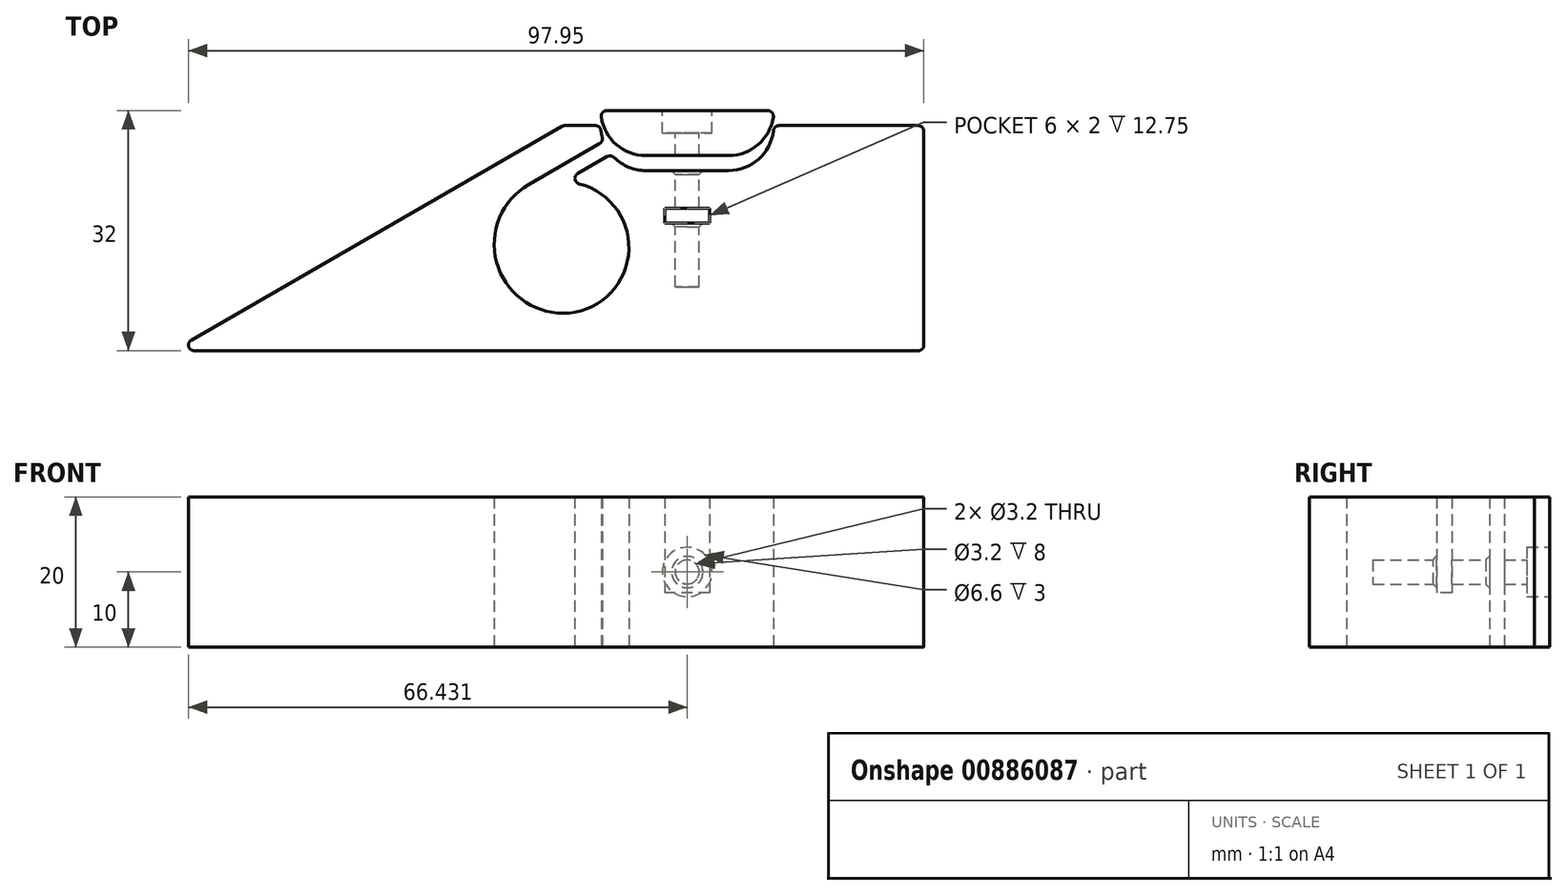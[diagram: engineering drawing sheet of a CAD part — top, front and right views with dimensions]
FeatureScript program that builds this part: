
annotation { "Feature Type Name" : "Feature", "Feature Type Description" : "" }
export const myFeature = defineFeature(function(context is Context, id is Id, definition is map)
    precondition{}
    {
        {
            assignVariable(context, id + "F0", {"name" : "distance", "anyValue" : 2});
        }
        {
            assignVariable(context, id + "F1", {"name" : "depth", "anyValue" : 20});
        }
        {
            assignVariable(context, id + "F2", {"name" : "squareNutWidth", "anyValue" : 5.5});
        }
        {
            var Q0;
            Q0=qCreatedBy(makeId("Top.planeOp"),FACE);
            var sketch = newSketch(context, id + "F3", { "sketchPlane" : qUnion([Q0])});
            skLineSegment(sketch, "E0", {"start": v(2.42, 1.4) * mm, "end": v(51.79, 29.9) * mm});
            skLineSegment(sketch, "E1", {"start": v(52.16, 30) * mm, "end": v(56.25, 30) * mm});
            skLineSegment(sketch, "E2", {"start": v(51.96, 30) * mm, "end": v(51.96, 0) * mm, "construction": true});
            skLineSegment(sketch, "E3", {"start": v(2.8, 0) * mm, "end": v(99.25, 0) * mm});
            skLineSegment(sketch, "E4", {"start": v(100, 0.75) * mm, "end": v(100, 29.25) * mm});
            skLineSegment(sketch, "E5", {"start": v(99.25, 30) * mm, "end": v(80.7, 30) * mm});
            skArc(sketch, "E6", {"start": v(57, 29.33) * mm, "mid": v(57.07, 28.89) * mm, "end": v(57.17, 28.45) * mm});
            skArc(sketch, "E7", {"start": v(74, 24) * mm, "mid": v(78, 25.53) * mm, "end": v(79.96, 29.33) * mm});
            skPoint(sketch, "E8.centerSnap0", {"position": v(100, 15) * mm});
            skPoint(sketch, "E8.centerSnap1", {"position": v(90, 30) * mm});
            skLineSegment(sketch, "E9", {"start": v(62.96, 24) * mm, "end": v(74, 24) * mm});
            skLineSegment(sketch, "E10", {"start": v(62.96, 30) * mm, "end": v(11, 0) * mm, "construction": true});
            skLineSegment(sketch, "E11", {"start": v(56.82, 27.6) * mm, "end": v(50.96, 24.23) * mm});
            skLineSegment(sketch, "E12.MirrorCS", {"start": v(57.82, 25.87) * mm, "end": v(53.9, 23.6) * mm});
            skArc(sketch, "E13", {"start": v(51.96, 5) * mm, "mid": v(60.64, 12.68) * mm, "end": v(54.09, 22.23) * mm});
            skLineSegment(sketch, "E14", {"start": v(50.96, 24.23) * mm, "end": v(47.37, 22.15) * mm});
            skLineSegment(sketch, "E15", {"start": v(51.96, 5) * mm, "end": v(62.96, 5) * mm, "construction": true});
            skArc(sketch, "E16", {"start": v(47.37, 22.15) * mm, "mid": v(43.08, 11.81) * mm, "end": v(51.96, 5) * mm});
            skArc(sketch, "E17.trimOffspring", {"start": v(58.72, 25.76) * mm, "mid": v(60.67, 24.46) * mm, "end": v(62.96, 24) * mm});
            skPoint(sketch, "E18.visualSharp", {"position": v(0, 0) * mm});
            skArc(sketch, "E18.filletArc", {"start": v(2.42, 1.4) * mm, "mid": v(2.07, 0.56) * mm, "end": v(2.8, 0) * mm});
            skPoint(sketch, "E19.visualSharp", {"position": v(100, 0) * mm});
            skArc(sketch, "E19.filletArc", {"start": v(99.25, 0) * mm, "mid": v(99.78, 0.22) * mm, "end": v(100, 0.75) * mm});
            skPoint(sketch, "E20.visualSharp", {"position": v(100, 30) * mm});
            skArc(sketch, "E20.filletArc", {"start": v(100, 29.25) * mm, "mid": v(99.78, 29.78) * mm, "end": v(99.25, 30) * mm});
            skPoint(sketch, "E21.visualSharp", {"position": v(80, 30) * mm});
            skArc(sketch, "E21.filletArc", {"start": v(80.7, 30) * mm, "mid": v(80.2, 29.8) * mm, "end": v(79.96, 29.33) * mm});
            skPoint(sketch, "E22.visualSharp", {"position": v(56.96, 30) * mm});
            skArc(sketch, "E22.filletArc", {"start": v(57, 29.33) * mm, "mid": v(56.75, 29.8) * mm, "end": v(56.25, 30) * mm});
            skPoint(sketch, "E23.visualSharp", {"position": v(51.96, 30) * mm});
            skArc(sketch, "E23.filletArc", {"start": v(52.16, 30) * mm, "mid": v(51.97, 29.97) * mm, "end": v(51.79, 29.9) * mm});
            skLineSegment(sketch, "E24", {"start": v(68.48, 24) * mm, "end": v(68.48, 0) * mm, "construction": true});
            skLineSegment(sketch, "E25.bottom", {"start": v(71.48, 19) * mm, "end": v(65.48, 19) * mm});
            skLineSegment(sketch, "E25.top", {"start": v(71.48, 17) * mm, "end": v(65.48, 17) * mm});
            skLineSegment(sketch, "E25.left", {"start": v(71.48, 19) * mm, "end": v(71.48, 17) * mm});
            skLineSegment(sketch, "E25.right", {"start": v(65.48, 19) * mm, "end": v(65.48, 17) * mm});
            skPoint(sketch, "E25.middle", {"position": v(68.48, 18) * mm});
            skPoint(sketch, "E26.visualSharp", {"position": v(57.34, 27.9) * mm});
            skArc(sketch, "E26.filletArc", {"start": v(56.82, 27.6) * mm, "mid": v(57.13, 27.97) * mm, "end": v(57.17, 28.45) * mm});
            skPoint(sketch, "E27.visualSharp", {"position": v(58.34, 26.18) * mm});
            skArc(sketch, "E27.filletArc", {"start": v(58.72, 25.76) * mm, "mid": v(58.29, 25.97) * mm, "end": v(57.82, 25.87) * mm});
            skPoint(sketch, "E28.visualSharp", {"position": v(51.96, 22.5) * mm});
            skArc(sketch, "E28.filletArc", {"start": v(53.9, 23.6) * mm, "mid": v(53.53, 22.86) * mm, "end": v(54.09, 22.23) * mm});
            skLineSegment(sketch, "E29.0", {"start": v(62.96, 26) * mm, "end": v(74, 26) * mm});
            skLineSegment(sketch, "E30", {"start": v(57.77, 32) * mm, "end": v(79.2, 32) * mm});
            skArc(sketch, "E31", {"start": v(57.02, 31.14) * mm, "mid": v(59.03, 27.46) * mm, "end": v(62.96, 26) * mm});
            skArc(sketch, "E32", {"start": v(74, 26) * mm, "mid": v(77.93, 27.46) * mm, "end": v(79.94, 31.14) * mm});
            skPoint(sketch, "E33.visualSharp", {"position": v(56.96, 32) * mm});
            skArc(sketch, "E33.filletArc", {"start": v(57.77, 32) * mm, "mid": v(57.2, 31.74) * mm, "end": v(57.02, 31.14) * mm});
            skPoint(sketch, "E34.visualSharp", {"position": v(80, 32) * mm});
            skArc(sketch, "E34.filletArc", {"start": v(79.94, 31.14) * mm, "mid": v(79.76, 31.74) * mm, "end": v(79.2, 32) * mm});
            skSolve(sketch);
        }
        {
            var Q0;
            Q0 = qSketchRegion(id + "F3", true);
            extrude(context, id + "F4", {"entities" : qUnion([Q0]), "depth" : (getVariable(context, 'depth')) * mm, "offsetDistance" : 25 * mm});
        }
        {
            var Q0;
            Q0=makeQuery(id+"F3.imprint","IMPRINT",FACE,{"disambiguationData":[TD([[makeQuery(id+"F3.imprint","IMPRINT",EDGE,{"derivedFrom":sQuery(id+"F3.wireOp",EDGE,"E25.bottom")}),1.0]])]});
            extrude(context, id + "F5", {"entities" : qUnion([Q0]), "operationType" : NewBodyOperationType.ADD, "depth" : ((getVariable(context, 'depth') - getVariable(context, 'squareNutWidth')) / 2) * mm, "offsetDistance" : 25 * mm});
        }
        {
            var Q0;
            Q0=makeQuery(id+"F4.opExtrude","SWEPT_FACE",FACE,{"disambiguationData":[OSD([sQuery(id+"F3.wireOp",EDGE,"E30")])]});
            var sketch = newSketch(context, id + "F6", { "sketchPlane" : qUnion([Q0])});
            skCircle(sketch, "E35", {"center": v(-68.48, 10) * mm, "radius": 1.6 * mm});
            skPoint(sketch, "E35.centerSnap1", {"position": v(-68.48, 0) * mm});
            skCircle(sketch, "E36", {"center": v(-68.48, 10) * mm, "radius": 3.3 * mm});
            skPoint(sketch, "E37", {"position": v(-57.77, 10) * mm});
            skSolve(sketch);
        }
        {
            var Q0;
            Q0 = qSketchRegion(id + "F6", true);
            extrude(context, id + "F7", {"entities" : qUnion([Q0]), "operationType" : NewBodyOperationType.REMOVE, "oppositeDirection" : true, "depth" : 3 * mm, "offsetDistance" : 25 * mm});
        }
        {
            var Q0;
            Q0=makeQuery(id+"F6.imprint","IMPRINT",FACE,{"disambiguationData":[TD([[makeQuery(id+"F6.imprint","IMPRINT",EDGE,{"derivedFrom":sQuery(id+"F6.wireOp",EDGE,"E35")}),1.0]])]});
            var Q1;
            Q1=makeQuery(id+"F4.opExtrude","SWEPT_FACE",FACE,{"disambiguationData":[OSD([sQuery(id+"F3.wireOp",EDGE,"E29.0")])]});
            extrude(context, id + "F8", {"entities" : qUnion([Q0]), "operationType" : NewBodyOperationType.REMOVE, "oppositeDirection" : true, "depth" : (21.5 + getVariable(context, 'distance')) * mm, "endBoundEntityFace" : qUnion([Q1]), "offsetDistance" : 25 * mm});
        }
        {
            var Q0;
            Q0=makeQuery(id+"F7.boolean.opBoolean","COPY",EDGE,{"derivedFrom":makeQuery(id+"F7.opExtrude","CAP_EDGE",EDGE,{"disambiguationData":[OSD([sQuery(id+"F6.wireOp",EDGE,"E36")])],"isStart":true})});
            var Q1;
            Q1=makeQuery(id+"F8.boolean.opBoolean","INTERSECT",EDGE,{"derivedFrom":[makeQuery(id+"F4.opExtrude","SWEPT_FACE",FACE,{"disambiguationData":[OSD([sQuery(id+"F3.wireOp",EDGE,"E9")])]}),makeQuery(id+"F8.opExtrude","SWEPT_FACE",FACE,{"disambiguationData":[OSD([sQuery(id+"F6.wireOp",EDGE,"E35")])]})]});
            var Q2;
            Q2=makeQuery(id+"F8.boolean.opBoolean","INTERSECT",EDGE,{"derivedFrom":[makeQuery(id+"F4.opExtrude","SWEPT_FACE",FACE,{"disambiguationData":[OSD([sQuery(id+"F3.wireOp",EDGE,"E25.top")])]}),makeQuery(id+"F8.opExtrude","SWEPT_FACE",FACE,{"disambiguationData":[OSD([sQuery(id+"F6.wireOp",EDGE,"E35")])]})]});
            chamfer(context, id + "F9", {"entities" : qUnion([Q0, Q1, Q2]), "width" : .5 * mm, "tangentPropagation" : true});
        }
    });
